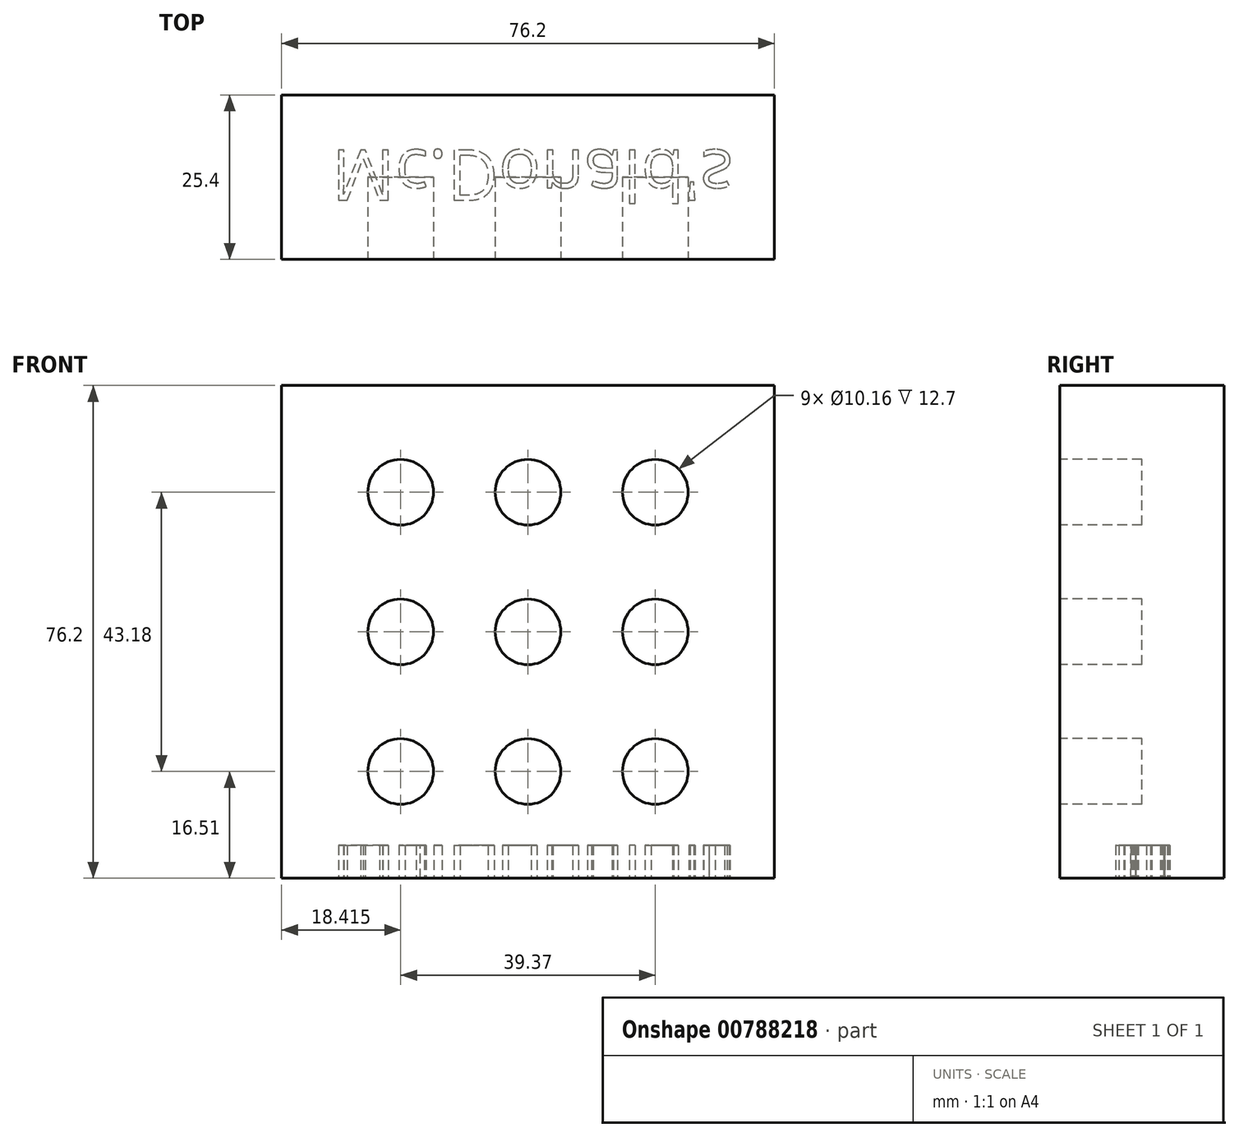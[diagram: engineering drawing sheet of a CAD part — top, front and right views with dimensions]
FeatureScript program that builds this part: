
annotation { "Feature Type Name" : "Feature", "Feature Type Description" : "" }
export const myFeature = defineFeature(function(context is Context, id is Id, definition is map)
    precondition{}
    {
        {
            var Q0;
            Q0=qCreatedBy(makeId("Front.planeOp"),FACE);
            var sketch = newSketch(context, id + "F0", { "sketchPlane" : qUnion([Q0])});
            skLineSegment(sketch, "E0.bottom", {"start": v(0, 0) * mm, "end": v(76.2, 0) * mm});
            skLineSegment(sketch, "E0.top", {"start": v(0, 76.2) * mm, "end": v(76.2, 76.2) * mm});
            skLineSegment(sketch, "E0.left", {"start": v(0, 0) * mm, "end": v(0, 76.2) * mm});
            skLineSegment(sketch, "E0.right", {"start": v(76.2, 0) * mm, "end": v(76.2, 76.2) * mm});
            skSolve(sketch);
        }
        {
            var Q0;
            Q0 = qSketchRegion(id + "F0", true);
            extrude(context, id + "F1", {"entities" : qUnion([Q0]), "depth" : 25.4 * mm, "offsetDistance" : 25.4 * mm});
        }
        {
            var Q0;
            Q0=makeQuery(id+"F1.opExtrude","CAP_FACE",FACE,{"disambiguationData":[OSD([sQuery(id+"F0.wireOp",EDGE,"E0.bottom"),sQuery(id+"F0.wireOp",EDGE,"E0.top"),sQuery(id+"F0.wireOp",EDGE,"E0.left"),sQuery(id+"F0.wireOp",EDGE,"E0.right")])],"isStart":false});
            var sketch = newSketch(context, id + "F2", { "sketchPlane" : qUnion([Q0])});
            skCircle(sketch, "E1", {"center": v(18.41, 59.7) * mm, "radius": 5.08 * mm});
            skCircle(sketch, "E2", {"center": v(18.41, 38.1) * mm, "radius": 5.08 * mm});
            skCircle(sketch, "E3", {"center": v(18.41, 16.51) * mm, "radius": 5.08 * mm});
            skCircle(sketch, "E4", {"center": v(38.1, 59.7) * mm, "radius": 5.08 * mm});
            skCircle(sketch, "E5", {"center": v(38.1, 38.1) * mm, "radius": 5.08 * mm});
            skCircle(sketch, "E6", {"center": v(38.1, 16.51) * mm, "radius": 5.08 * mm});
            skCircle(sketch, "E7", {"center": v(57.79, 59.69) * mm, "radius": 5.08 * mm});
            skCircle(sketch, "E8", {"center": v(57.79, 38.1) * mm, "radius": 5.08 * mm});
            skCircle(sketch, "E9", {"center": v(57.79, 16.51) * mm, "radius": 5.08 * mm});
            skSolve(sketch);
        }
        {
            var Q0;
            Q0=makeQuery(id+"F1.opExtrude","SWEPT_FACE",FACE,{"disambiguationData":[OSD([sQuery(id+"F0.wireOp",EDGE,"E0.bottom")])]});
            var sketch = newSketch(context, id + "F3", { "sketchPlane" : qUnion([Q0])});
            skText(sketch, "E10", { "text": "Mc.Donald\'s", "fontName": "OpenSans-Regular.ttf"});
            const initialGuessF3  = {"E10": [0.00773, 0.0085, 1, 0, 0.00783]};
            skSetInitialGuess(sketch, initialGuessF3);
            skSolve(sketch);
        }
        {
            var Q0;
            Q0 = qSketchRegion(id + "F2", true);
            extrude(context, id + "F4", {"entities" : qUnion([Q0]), "operationType" : NewBodyOperationType.REMOVE, "oppositeDirection" : true, "depth" : 12.7 * mm, "offsetDistance" : 25.4 * mm});
        }
        {
            var Q0;
            Q0 = qSketchRegion(id + "F3", true);
            extrude(context, id + "F5", {"entities" : qUnion([Q0]), "operationType" : NewBodyOperationType.REMOVE, "oppositeDirection" : true, "depth" : 5.08 * mm, "offsetDistance" : 25.4 * mm});
        }
    });
